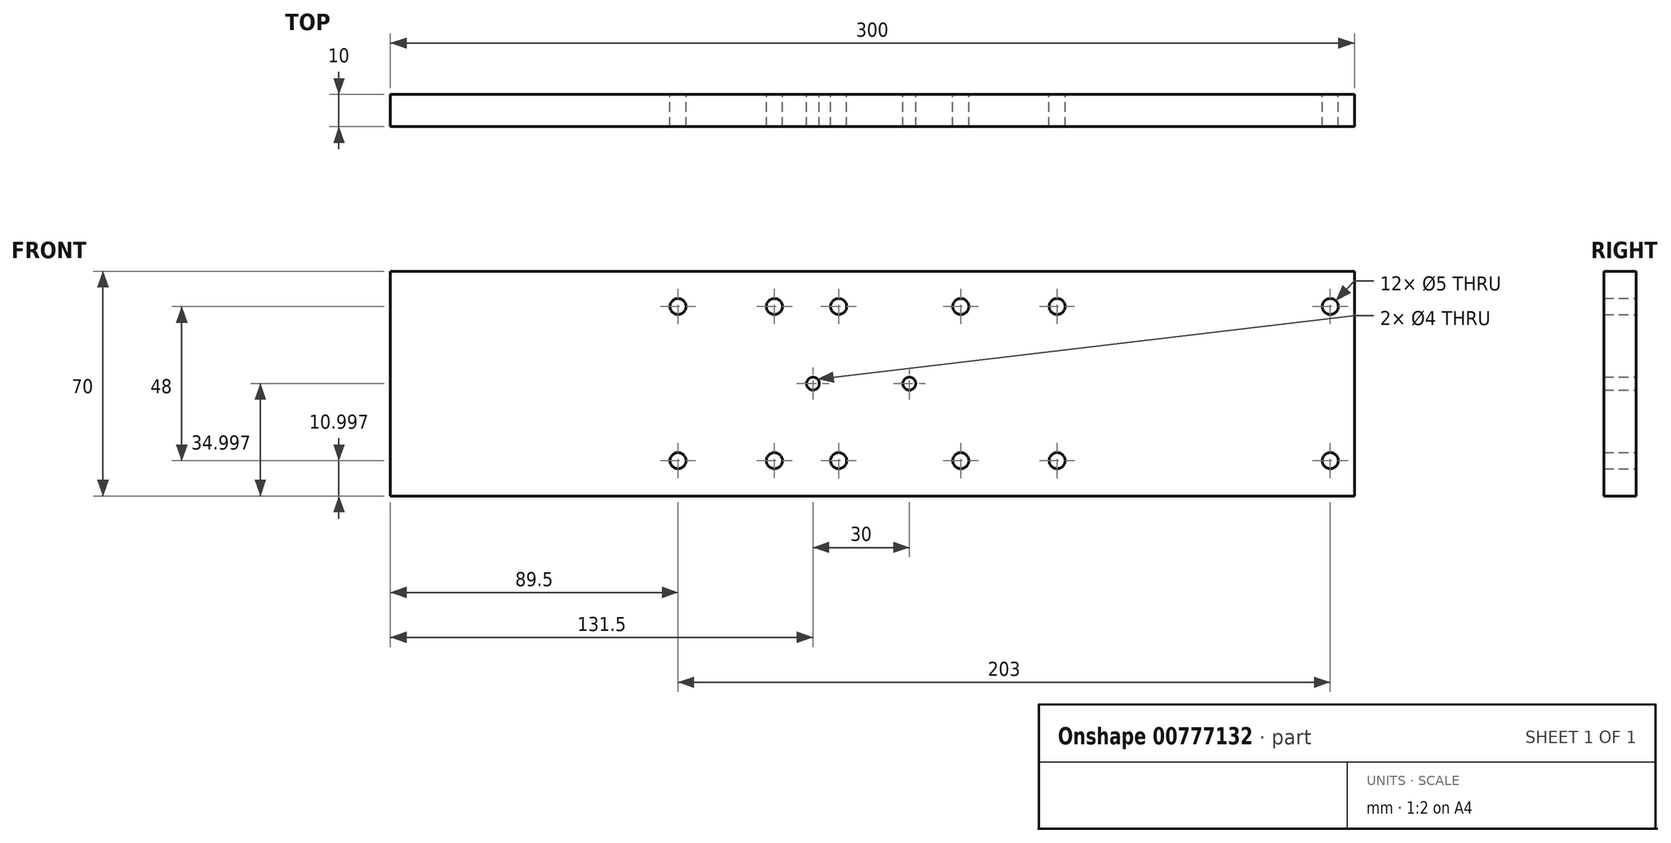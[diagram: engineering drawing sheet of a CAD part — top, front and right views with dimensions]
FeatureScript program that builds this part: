
annotation { "Feature Type Name" : "Feature", "Feature Type Description" : "" }
export const myFeature = defineFeature(function(context is Context, id is Id, definition is map)
    precondition{}
    {
        {
            var Q0;
            Q0=qCreatedBy(makeId("Front.planeOp"),FACE);
            var sketch = newSketch(context, id + "F0", { "sketchPlane" : qUnion([Q0])});
            skLineSegment(sketch, "E0.bottom", {"start": v(-119.5, 51.28) * mm, "end": v(180.5, 51.28) * mm});
            skLineSegment(sketch, "E0.top", {"start": v(-119.5, -18.72) * mm, "end": v(180.5, -18.72) * mm});
            skLineSegment(sketch, "E0.left", {"start": v(-119.5, 51.28) * mm, "end": v(-119.5, -18.72) * mm});
            skLineSegment(sketch, "E0.right", {"start": v(180.5, 51.28) * mm, "end": v(180.5, -18.72) * mm});
            skCircle(sketch, "E1", {"center": v(88, 40.28) * mm, "radius": 2.5 * mm});
            skCircle(sketch, "E2", {"center": v(88, -7.72) * mm, "radius": 2.5 * mm});
            skCircle(sketch, "E3", {"center": v(58, 40.28) * mm, "radius": 2.5 * mm});
            skCircle(sketch, "E4", {"center": v(173, 40.28) * mm, "radius": 2.5 * mm});
            skCircle(sketch, "E5", {"center": v(20, 40.28) * mm, "radius": 2.5 * mm});
            skCircle(sketch, "E6", {"center": v(0, 40.28) * mm, "radius": 2.5 * mm});
            skCircle(sketch, "E7", {"center": v(-30, 40.28) * mm, "radius": 2.5 * mm});
            skCircle(sketch, "E8", {"center": v(58, -7.72) * mm, "radius": 2.5 * mm});
            skCircle(sketch, "E9", {"center": v(173, -7.72) * mm, "radius": 2.5 * mm});
            skCircle(sketch, "E10", {"center": v(20, -7.72) * mm, "radius": 2.5 * mm});
            skCircle(sketch, "E11", {"center": v(0, -7.72) * mm, "radius": 2.5 * mm});
            skCircle(sketch, "E12", {"center": v(-30, -7.72) * mm, "radius": 2.5 * mm});
            skCircle(sketch, "E13", {"center": v(12, 16.28) * mm, "radius": 2 * mm});
            skPoint(sketch, "E13.centerSnap0", {"position": v(-119.5, 16.28) * mm});
            skCircle(sketch, "E14", {"center": v(42, 16.28) * mm, "radius": 2 * mm});
            skSolve(sketch);
        }
        {
            var Q0;
            Q0 = qSketchRegion(id + "F0", true);
            extrude(context, id + "F1", {"entities" : qUnion([Q0]), "depth" : 10 * mm, "offsetDistance" : 25 * mm});
        }
    });
